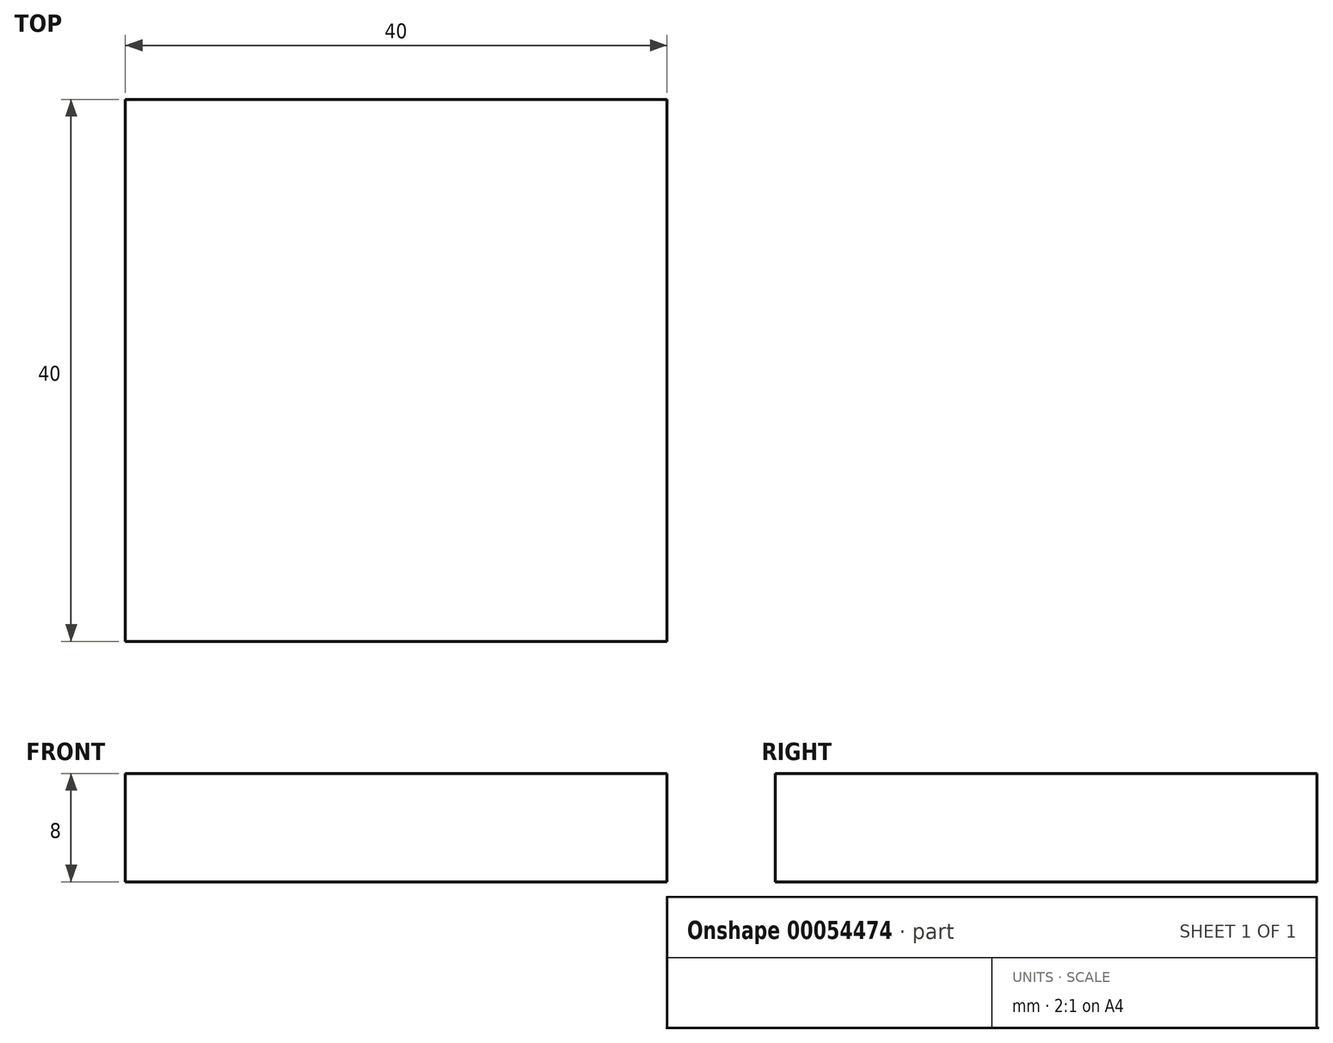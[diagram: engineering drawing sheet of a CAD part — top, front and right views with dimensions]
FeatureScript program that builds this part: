
annotation { "Feature Type Name" : "Feature", "Feature Type Description" : "" }
export const myFeature = defineFeature(function(context is Context, id is Id, definition is map)
    precondition{}
    {
        {
            var Q0;
            Q0=qCreatedBy(makeId("Top.planeOp"),FACE);
            var sketch = newSketch(context, id + "F0", { "sketchPlane" : qUnion([Q0])});
            skLineSegment(sketch, "E0.rect.bottom", {"start": v(20, -20) * mm, "end": v(-20, -20) * mm});
            skLineSegment(sketch, "E0.rect.top", {"start": v(20, 20) * mm, "end": v(-20, 20) * mm});
            skLineSegment(sketch, "E0.rect.left", {"start": v(20, -20) * mm, "end": v(20, 20) * mm});
            skLineSegment(sketch, "E0.rect.right", {"start": v(-20, -20) * mm, "end": v(-20, 20) * mm});
            skPoint(sketch, "E0.rect.middle", {"position": v(0, 0) * mm});
            skSolve(sketch);
        }
        {
            var Q0;
            Q0 = qSketchRegion(id + "F0", true);
            extrude(context, id + "F1", {"entities" : qUnion([Q0]), "depth" : 8 * mm});
        }
    });
